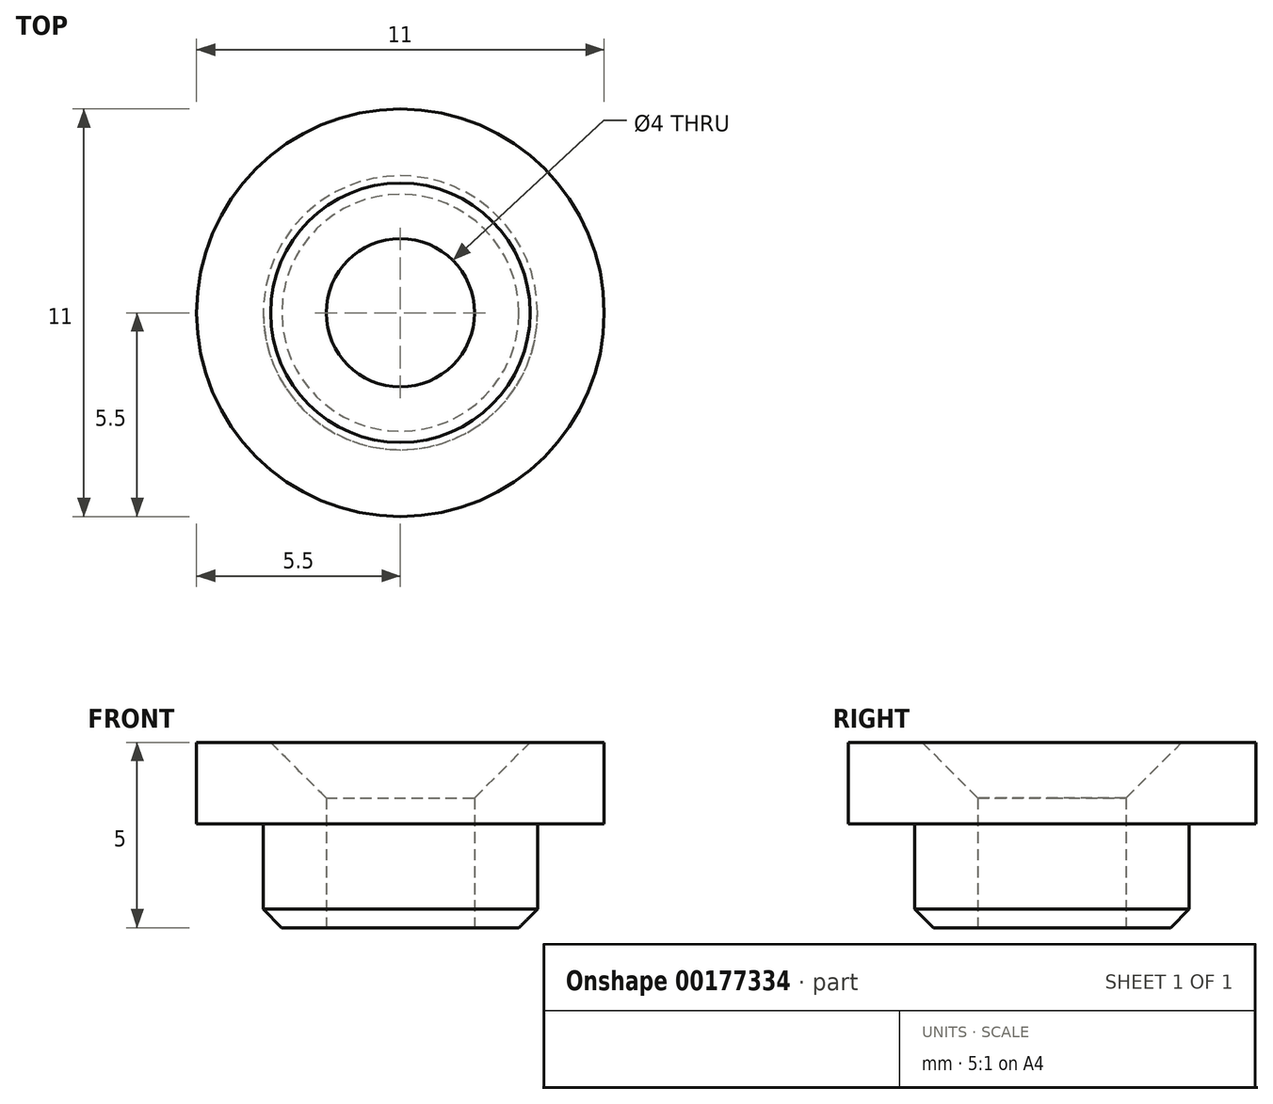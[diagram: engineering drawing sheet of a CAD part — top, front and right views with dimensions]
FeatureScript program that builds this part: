
annotation { "Feature Type Name" : "Feature", "Feature Type Description" : "" }
export const myFeature = defineFeature(function(context is Context, id is Id, definition is map)
    precondition{}
    {
        {
            var Q0;
            Q0=qCreatedBy(makeId("Right.planeOp"),FACE);
            var sketch = newSketch(context, id + "F0", { "sketchPlane" : qUnion([Q0])});
            skLineSegment(sketch, "E0", {"start": v(0, 0) * mm, "end": v(0, 9.24) * mm, "construction": true});
            skLineSegment(sketch, "E1", {"start": v(-2, 0) * mm, "end": v(-2, 5) * mm});
            skLineSegment(sketch, "E2", {"start": v(-2, 5) * mm, "end": v(-5.5, 5) * mm});
            skLineSegment(sketch, "E3", {"start": v(-5.5, 5) * mm, "end": v(-5.5, 2.8) * mm});
            skLineSegment(sketch, "E4", {"start": v(-5.5, 2.8) * mm, "end": v(-3.7, 2.8) * mm});
            skLineSegment(sketch, "E5", {"start": v(-3.7, 2.8) * mm, "end": v(-3.7, 0) * mm});
            skLineSegment(sketch, "E6", {"start": v(-3.7, 0) * mm, "end": v(-2, 0) * mm});
            skSolve(sketch);
        }
        {
            var Q0;
            Q0 = qSketchRegion(id + "F0", true);
            var Q1;
            Q1=sQuery(id+"F0.wireOp",EDGE,"E0");
            revolve(context, id + "F1", {"surfaceOperationType" : NewSurfaceOperationType.NEW, "entities" : qUnion([Q0]), "axis" : qUnion([Q1]), "revolveType" : RevolveType.FULL});
        }
        {
            var Q0;
            Q0=makeQuery(id+"F1.opRevolve","SWEPT_EDGE",EDGE,{"disambiguationData":[OSD([sQuery(id+"F0.wireOp",EDGE,"E1"),sQuery(id+"F0.wireOp",EDGE,"E2")])]});
            chamfer(context, id + "F2", {"entities" : qUnion([Q0]), "width" : 1.5 * mm, "tangentPropagation" : true});
        }
        {
            var Q0;
            Q0=makeQuery(id+"F1.opRevolve","SWEPT_EDGE",EDGE,{"disambiguationData":[OSD([sQuery(id+"F0.wireOp",EDGE,"E5"),sQuery(id+"F0.wireOp",EDGE,"E6")])]});
            chamfer(context, id + "F3", {"entities" : qUnion([Q0]), "width" : 0.5 * mm, "tangentPropagation" : true});
        }
    });
